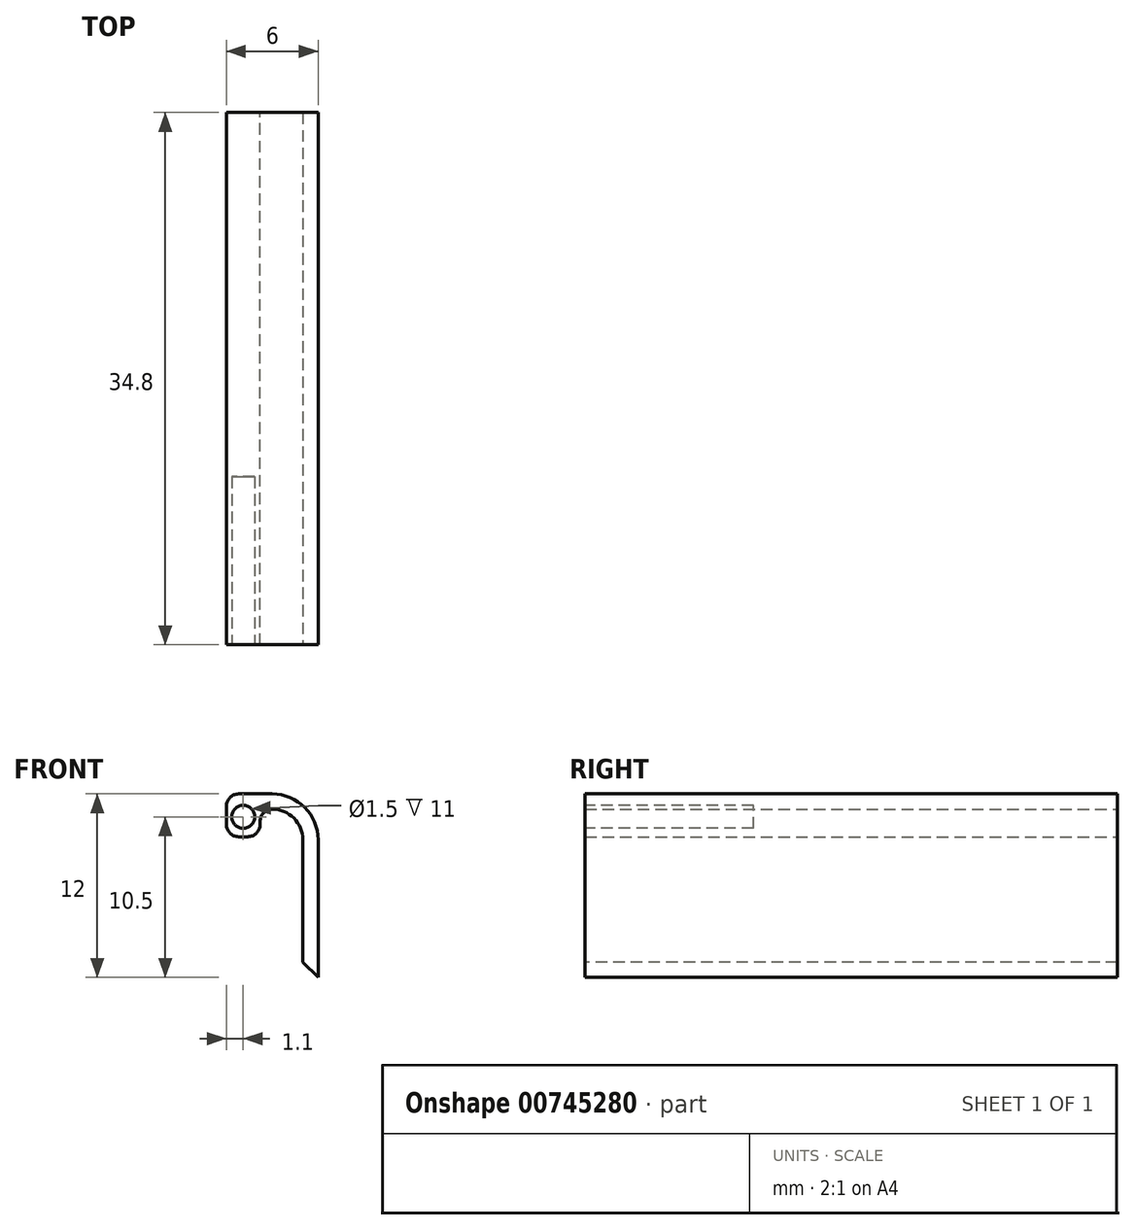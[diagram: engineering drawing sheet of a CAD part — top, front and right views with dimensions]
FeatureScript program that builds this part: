
annotation { "Feature Type Name" : "Feature", "Feature Type Description" : "" }
export const myFeature = defineFeature(function(context is Context, id is Id, definition is map)
    precondition{}
    {
        {
            var Q0;
            Q0=qCreatedBy(makeId("Front.planeOp"),FACE);
            var sketch = newSketch(context, id + "F0", { "sketchPlane" : qUnion([Q0])});
            skLineSegment(sketch, "E0", {"start": v(5, -3) * mm, "end": v(5, -12) * mm});
            skLineSegment(sketch, "E1", {"start": v(5, -12) * mm, "end": v(6, -12) * mm});
            skLineSegment(sketch, "E2", {"start": v(6, -12) * mm, "end": v(6, -3) * mm});
            skLineSegment(sketch, "E3", {"start": v(3, 0) * mm, "end": v(0, 0) * mm});
            skLineSegment(sketch, "E4", {"start": v(0, 0) * mm, "end": v(0, -2.8) * mm});
            skArc(sketch, "E5.filletArc", {"start": v(5, -3) * mm, "mid": v(4.41, -1.59) * mm, "end": v(3, -1) * mm});
            skArc(sketch, "E6.filletArc", {"start": v(6, -3) * mm, "mid": v(5.12, -0.88) * mm, "end": v(3, 0) * mm});
            skLineSegment(sketch, "E7", {"start": v(3, 0) * mm, "end": v(3, -1) * mm, "construction": true});
            skLineSegment(sketch, "E8", {"start": v(0, -2.8) * mm, "end": v(2.2, -2.8) * mm});
            skLineSegment(sketch, "E9", {"start": v(2.2, -2.8) * mm, "end": v(2.2, -1) * mm});
            skLineSegment(sketch, "E10", {"start": v(2.2, -1) * mm, "end": v(3, -1) * mm});
            skSolve(sketch);
        }
        {
            var Q0;
            Q0 = qSketchRegion(id + "F0", true);
            extrude(context, id + "F1", {"entities" : qUnion([Q0]), "endBound" : BoundingType.SYMMETRIC, "depth" : 34.8 * mm, "offsetDistance" : 25 * mm});
        }
        {
            var Q0;
            Q0=makeQuery(id+"F1.opExtrude","CAP_FACE",FACE,{"disambiguationData":[OSD([sQuery(id+"F0.wireOp",EDGE,"E0"),sQuery(id+"F0.wireOp",EDGE,"E1"),sQuery(id+"F0.wireOp",EDGE,"E2"),sQuery(id+"F0.wireOp",EDGE,"E3"),sQuery(id+"F0.wireOp",EDGE,"E4"),sQuery(id+"F0.wireOp",EDGE,"E5.filletArc"),sQuery(id+"F0.wireOp",EDGE,"E6.filletArc"),sQuery(id+"F0.wireOp",EDGE,"E8"),sQuery(id+"F0.wireOp",EDGE,"E9"),sQuery(id+"F0.wireOp",EDGE,"E10")])],"isStart":false});
            var sketch = newSketch(context, id + "F2", { "sketchPlane" : qUnion([Q0])});
            skCircle(sketch, "E11", {"center": v(1.1, -1.5) * mm, "radius": 0.75 * mm});
            skSolve(sketch);
        }
        {
            var Q0;
            Q0 = qSketchRegion(id + "F2", true);
            extrude(context, id + "F3", {"entities" : qUnion([Q0]), "operationType" : NewBodyOperationType.REMOVE, "oppositeDirection" : true, "depth" : 11 * mm, "offsetDistance" : 25 * mm});
        }
        {
            var Q0;
            Q0=makeQuery(id+"F1.opExtrude","SWEPT_EDGE",EDGE,{"disambiguationData":[OSD([sQuery(id+"F0.wireOp",EDGE,"E9"),sQuery(id+"F0.wireOp",EDGE,"E10")])]});
            var Q1;
            Q1=makeQuery(id+"F1.opExtrude","SWEPT_EDGE",EDGE,{"disambiguationData":[OSD([sQuery(id+"F0.wireOp",EDGE,"E8"),sQuery(id+"F0.wireOp",EDGE,"E9")])]});
            var Q2;
            Q2=makeQuery(id+"F1.opExtrude","SWEPT_EDGE",EDGE,{"disambiguationData":[OSD([sQuery(id+"F0.wireOp",EDGE,"E4"),sQuery(id+"F0.wireOp",EDGE,"E8")])]});
            var Q3;
            Q3=makeQuery(id+"F1.opExtrude","SWEPT_EDGE",EDGE,{"disambiguationData":[OSD([sQuery(id+"F0.wireOp",EDGE,"E3"),sQuery(id+"F0.wireOp",EDGE,"E4")])]});
            fillet(context, id + "F4", {"entities" : qUnion([Q0, Q1, Q2, Q3]), "radius" : 0.8 * mm, "tangentPropagation" : true, "allowEdgeOverflow" : false});
        }
        {
            var Q0;
            Q0=makeQuery(id+"F1.opExtrude","SWEPT_EDGE",EDGE,{"disambiguationData":[OSD([sQuery(id+"F0.wireOp",EDGE,"E0"),sQuery(id+"F0.wireOp",EDGE,"E1")])]});
            chamfer(context, id + "F5", {"entities" : qUnion([Q0]), "width" : 1 * mm, "tangentPropagation" : true});
        }
    });
